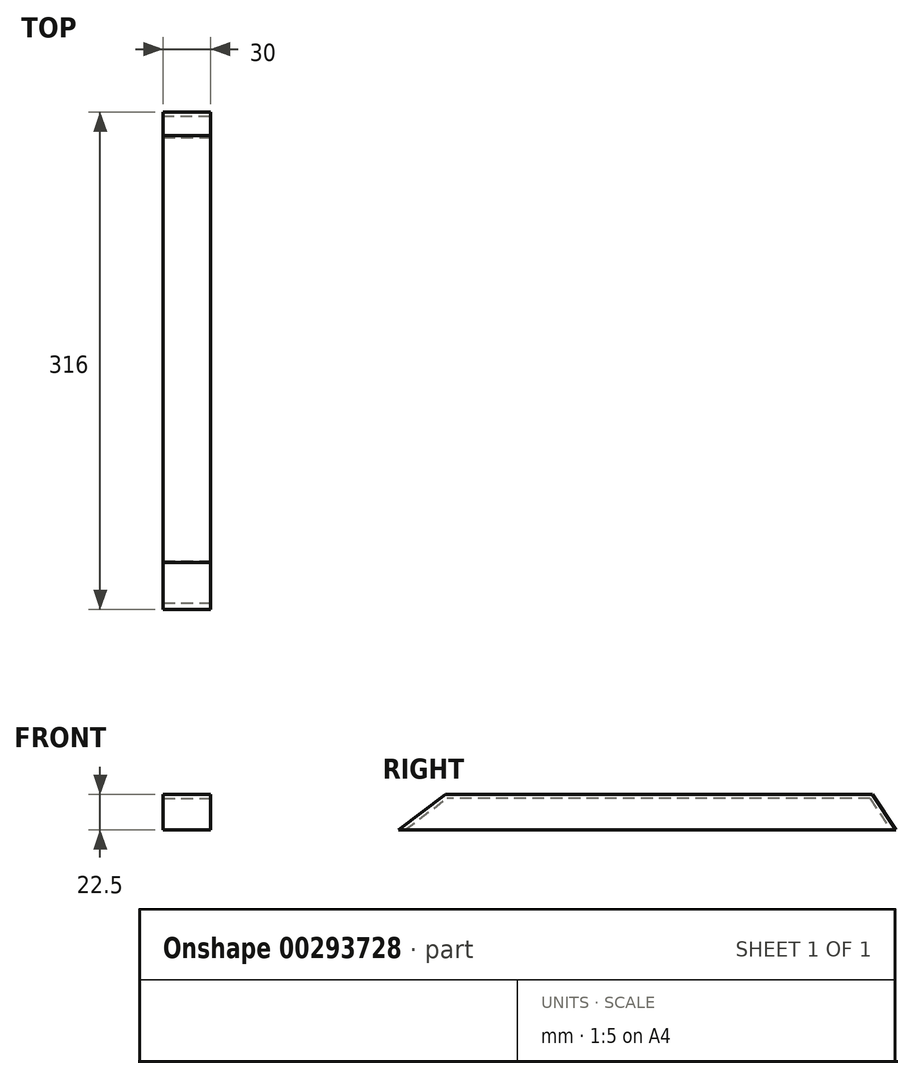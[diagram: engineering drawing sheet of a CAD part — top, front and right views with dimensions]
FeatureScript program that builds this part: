
annotation { "Feature Type Name" : "Feature", "Feature Type Description" : "" }
export const myFeature = defineFeature(function(context is Context, id is Id, definition is map)
    precondition{}
    {
        {
            var Q0;
            Q0=qCreatedBy(makeId("Top.planeOp"),FACE);
            var sketch = newSketch(context, id + "F0", { "sketchPlane" : qUnion([Q0])});
            skLineSegment(sketch, "E0.bottom", {"start": v(-15, 158) * mm, "end": v(15, 158) * mm});
            skLineSegment(sketch, "E0.top", {"start": v(-15, -158) * mm, "end": v(15, -158) * mm});
            skLineSegment(sketch, "E0.left", {"start": v(-15, 158) * mm, "end": v(-15, -158) * mm});
            skLineSegment(sketch, "E0.right", {"start": v(15, 158) * mm, "end": v(15, -158) * mm});
            skPoint(sketch, "E0.middle", {"position": v(0, 0) * mm});
            skSolve(sketch);
        }
        {
            var Q0;
            Q0 = qSketchRegion(id + "F0", true);
            extrude(context, id + "F1", {"entities" : qUnion([Q0]), "depth" : 5 * mm});
        }
        {
            var Q0;
            Q0=makeQuery(id+"F1.opExtrude","CAP_FACE",FACE,{"disambiguationData":[OSD([sQuery(id+"F0.wireOp",EDGE,"E0.bottom"),sQuery(id+"F0.wireOp",EDGE,"E0.top"),sQuery(id+"F0.wireOp",EDGE,"E0.left"),sQuery(id+"F0.wireOp",EDGE,"E0.right")])],"isStart":true});
            extrude(context, id + "F2", {"entities" : qUnion([Q0]), "operationType" : NewBodyOperationType.ADD, "depth" : 17.5 * mm});
        }
        {
            var Q0;
            Q0=makeQuery(id+"F1.opExtrude","CAP_EDGE",EDGE,{"disambiguationData":[OSD([sQuery(id+"F0.wireOp",EDGE,"E0.bottom")])],"isStart":false});
            chamfer(context, id + "F3", {"entities" : qUnion([Q0]), "chamferType" : ChamferType.TWO_OFFSETS, "width1" : 22.5 * mm, "oppositeDirection" : false, "width2" : 15 * mm, "tangentPropagation" : true});
        }
        {
            var Q0;
            Q0=makeQuery(id+"F1.opExtrude","CAP_EDGE",EDGE,{"disambiguationData":[OSD([sQuery(id+"F0.wireOp",EDGE,"E0.top")])],"isStart":false});
            chamfer(context, id + "F4", {"entities" : qUnion([Q0]), "chamferType" : ChamferType.TWO_OFFSETS, "width1" : 30 * mm, "oppositeDirection" : false, "width2" : 22.5 * mm, "tangentPropagation" : true});
        }
        {
            var Q0;
            Q0=makeQuery(id+"F2.opExtrude","CAP_FACE",FACE,{"disambiguationData":[OSD([sQuery(id+"F0.wireOp",EDGE,"E0.bottom"),sQuery(id+"F0.wireOp",EDGE,"E0.top"),sQuery(id+"F0.wireOp",EDGE,"E0.left"),sQuery(id+"F0.wireOp",EDGE,"E0.right")])],"isStart":false});
            shell(context, id + "F5", {"entities" : qUnion([Q0]), "thickness" : 2.5 * mm});
        }
        {
            var Q0;
            Q0=makeQuery(id+"F5.opShell","OFFSET_FACE",FACE,{"disambiguationData":[OSD([sQuery(id+"F0.wireOp",EDGE,"E0.left")])]});
            extrude(context, id + "F6", {"entities" : qUnion([Q0]), "operationType" : NewBodyOperationType.REMOVE, "oppositeDirection" : true, "depth" : 25 * mm});
        }
        {
            var Q0;
            Q0=makeQuery(id+"F5.opShell","OFFSET_FACE",FACE,{"disambiguationData":[OSD([sQuery(id+"F0.wireOp",EDGE,"E0.right")])]});
            extrude(context, id + "F7", {"entities" : qUnion([Q0]), "operationType" : NewBodyOperationType.REMOVE, "oppositeDirection" : true, "depth" : 2.4 * mm});
        }
    });
